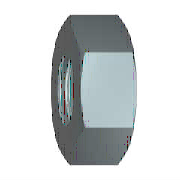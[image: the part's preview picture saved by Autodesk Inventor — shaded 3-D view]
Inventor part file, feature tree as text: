
AUTODESK INVENTOR PART (.ipt)
format: ipt  version: 2023.2 (Build 272271030, 271C)  size: 172,032 bytes
history: native  units: mm (DEFAULTED — no unit token found)
features: sketch x3, chamfer x1, hole x1, other x1, plane x1
ambient origin geometry x7: Origin, YZ Plane, XZ Plane, X Axis, Y Axis, Z Axis, Center Point
bodies: Solid1 (feature_tree), Body (feature_tree)
feature tree (7):
  chamfer  "Chamfer1"  Angle=30.0deg  [1 undecoded]
  hole  "Thread"  [1 undecoded]
  other  "Work Axis1"
  plane  "Work Plane1"
  sketch  "Sketch1"  dims[d0=24.248711mm]
  sketch  "Sketch2"  dims[d1=14.1mm]
  sketch  "Sketch3"  dims[d2=0.0mm d3=30.0deg d4=30.0deg d5=21.0mm d6=21.0mm d7=90.0deg d25=11.835mm d26=6.0mm d27=4.0mm d28=2.0mm d29=14.3117mm d30=8.0mm d31=20.594885mm d8=1.082532mm d9=30.0deg d10=1.082532mm d11=30.0deg d13=0.0mm d14=0.0mm d39=0.0mm d40=1.082532mm d41=1.082532mm d42=0.0mm]
note: 2 required parameter values undecoded (feature->parameter linkage not recoverable at this tier; creation-order binding heuristic only, values carry confidence <= 0.55)
